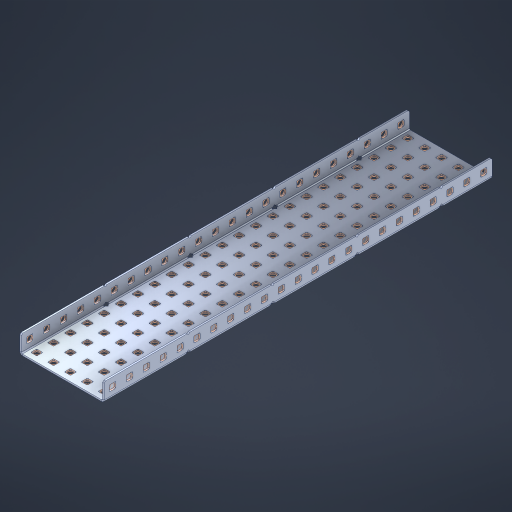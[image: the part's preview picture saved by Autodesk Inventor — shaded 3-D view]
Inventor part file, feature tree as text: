
AUTODESK INVENTOR PART (.ipt)
format: ipt  version: 2023 (Build 270158000, 158)  size: 1,823,744 bytes
history: native  units: in
note: dims shown in document units (in); Inventor stores cm internally (conversion verified against a paired STEP export)
features: other x166, extrude x160, sheet_metal_op x10, sketch x8, mirror x1, pattern_linear x1, chamfer x1
ambient origin geometry x8: Origin, YZ Plane, XZ Plane, XY Plane, X Axis, Y Axis, Z Axis, Center Point
bodies: Solid1 (feature_tree), Body (feature_tree)
feature tree (347):
  other  "Flange Pattern Plane"
  sheet_metal_op  "Flange Pattern"
  sheet_metal_op  "Body Pattern"
  other  "Arc Length"
  mirror  "Notch Mirror"
  pattern_linear  "Notch Pattern"  Spacing1=0.1875in  [1 undecoded]
  chamfer  "End Chamfer"
  extrude  "Half Cut"  Depth=0.0469in
  sketch  "Sketch1"  dims[d0=2.5in]
  other  "Plate1"
  sketch  "Sketch2"  dims[d1=11.5in]
  other  "Plate2"
  sheet_metal_op  "Bend1"
  sheet_metal_op  "Corner1"
  sketch  "Sketch3"  dims[d2=0.0469in]
  other  "Flange Pattern Sketch"
  sketch  "Sketch7"  dims[d3=0.0469in]
  other  "Srf1"
  other  "Srf2"
  sketch  "Sketch8"  dims[d4=0.0234in]
  sketch  "Sketch9"  dims[d5=0.0938in]
  other  "Srf91"
  sheet_metal_op  "Body Pattern Sketch"
  other  "Srf92"
  sketch  "Sketch13"  dims[d6=0.0469in]
  sketch  "Sketch14"  dims[d7=0.5in d8=90.0deg d9=0.0312in d10=0.1875in d11=0.0469in d12=0.0469in d16=0.182in d17=0.02in d18=0.0469in d19=0.0in d20=0.25in d21=0.25in d46=0.172in d47=1.0in d48=0.0in d49=0.182in d50=0.02in d51=0.25in d52=0.25in d53=0.0469in d54=0.0in d55=0.172in d56=1.0in d57=0.0in d60=9.0551in d62=0.5in d63=1.9685in d65=0.5in d85=0.1227in d86=0.1659in d88=0.04in d89=0.0469in d90=0.0in d91=0.04in d92=0.0491in d95=2.5in d96=0.04in d97=0.25in d98=45.0deg d101=0.0in d102=2.497in d131=2.5in d132=9.0551in d134=0.5in d139=0.5in]
  other  "Srf856"
  other  "Srf1310"
  other  "Srf1311"
  other  "Srf1312"
  other  "Srf1376"
  other  "Srf1377"
  other  "Srf1728"
  other  "Srf1755"
  other  "Srf1878"
  other  "Srf1879"
  other  "Srf1880"
  other  "Srf1881"
  other  "Srf1882"
  other  "Srf1883"
  other  "Srf1884"
  other  "Srf1885"
  other  "Srf1886"
  other  "Srf1887"
  other  "Srf1888"
  other  "Srf1889"
  other  "Srf1890"
  other  "Srf1891"
  other  "Srf1892"
  other  "Srf1893"
  other  "Srf1894"
  other  "Srf1895"
  other  "Srf1896"
  other  "Srf1897"
  other  "Srf1898"
  other  "Srf1899"
  other  "Srf1900"
  other  "Srf1901"
  other  "Srf1902"
  other  "Srf1903"
  other  "Srf1904"
  other  "Srf1905"
  other  "Srf1906"
  other  "Srf1942"
  other  "Srf1943"
  other  "Srf1944"
  other  "Srf1945"
  other  "Srf1946"
  other  "Srf1947"
  other  "Srf1948"
  other  "Srf1949"
  other  "Srf1950"
  other  "Srf1951"
  other  "Srf1952"
  other  "Srf1953"
  other  "Srf1954"
  other  "Srf1955"
  other  "Srf1956"
  other  "Srf1957"
  other  "Srf1958"
  other  "Srf1959"
  other  "Srf1960"
  other  "Srf1961"
  other  "Srf1962"
  other  "Srf1963"
  other  "Srf1964"
  other  "Srf1965"
  other  "Srf1966"
  other  "Srf1967"
  other  "Srf1968"
  other  "Srf1969"
  other  "Srf1970"
  other  "Srf2111"
  other  "Srf2112"
  other  "Srf2113"
  other  "Srf2114"
  other  "Srf2115"
  other  "Srf2116"
  other  "Srf2117"
  other  "Srf2118"
  other  "Srf2119"
  other  "Srf2120"
  other  "Srf2121"
  other  "Srf2146"
  other  "Srf2147"
  other  "Srf2148"
  other  "Srf2149"
  other  "Srf2150"
  other  "Srf2151"
  other  "Srf2152"
  other  "Srf2153"
  other  "Srf2154"
  other  "Srf2155"
  other  "Srf2156"
  other  "Srf2157"
  other  "Srf2158"
  other  "Srf2159"
  other  "Srf2160"
  other  "Srf2161"
  other  "Srf2162"
  other  "Srf2163"
  other  "Srf2164"
  other  "Srf2165"
  other  "Srf2166"
  other  "Srf2167"
  other  "Srf2168"
  other  "Srf2169"
  other  "Srf2170"
  other  "Srf2171"
  other  "Srf2172"
  other  "Srf2173"
  other  "Srf2174"
  other  "Srf2175"
  other  "Srf2176"
  other  "Srf2177"
  other  "Srf2178"
  other  "Srf2179"
  other  "Srf2180"
  other  "Srf2181"
  other  "Srf2182"
  other  "Srf2183"
  other  "Srf2184"
  other  "Srf2185"
  other  "Srf2186"
  other  "Srf2187"
  other  "Srf2188"
  other  "Srf2189"
  other  "Srf2190"
  other  "Srf2191"
  other  "Srf2192"
  other  "Srf2193"
  other  "Srf2194"
  other  "Srf2195"
  other  "Srf2196"
  other  "Srf2197"
  other  "Srf2198"
  other  "Srf2199"
  other  "Srf2200"
  other  "Srf2201"
  other  "Srf2202"
  other  "Srf2203"
  other  "Srf2204"
  other  "Srf2205"
  other  "Srf2206"
  other  "Srf2207"
  other  "Srf2208"
  other  "Srf2209"
  other  "Srf2210"
  other  "Srf2211"
  other  "Srf2212"
  other  "Srf2213"
  other  "Srf2214"
  other  "Srf2215"
  other  "Srf2216"
  other  "Srf2217"
  other  "Srf2218"
  other  "Srf2219"
  other  "Srf2220"
  other  "Srf2221"
  other  "Srf2222"
  other  "Srf2223"
  other  "Srf2224"
  other  "Srf2225"
  sheet_metal_op  "Flange Stamp"
  sheet_metal_op  "Flange Circle"
  sheet_metal_op  "Body Stamp"
  sheet_metal_op  "Body Circle"
  sheet_metal_op  "Notch"
  extrude  "ExtrusionSrf2"  Depth=0.0469in
  extrude  "ExtrusionSrf92"  Depth=2.5in
  extrude  "ExtrusionSrf856"  Depth=0.02in
  extrude  "ExtrusionSrf1310"  Depth=0.0469in
  extrude  "ExtrusionSrf1311"  TaperAngle=0.0deg  [1 undecoded]
  extrude  "ExtrusionSrf1312"  Depth=0.25in
  extrude  "ExtrusionSrf1376"  Depth=0.25in
  extrude  "ExtrusionSrf1377"  Depth=2.5in
  extrude  "ExtrusionSrf1728"  Depth=2.5in TaperAngle=0.0deg
  extrude  "ExtrusionSrf1755"  Depth=2.5in
  extrude  "ExtrusionSrf1878"  Depth=0.02in
  extrude  "ExtrusionSrf1879"  Depth=0.25in
  extrude  "ExtrusionSrf1880"  Depth=0.25in
  extrude  "ExtrusionSrf1881"  Depth=0.0469in
  extrude  "ExtrusionSrf1882"  TaperAngle=0.0deg  [1 undecoded]
  extrude  "ExtrusionSrf1883"  Depth=2.5in
  extrude  "ExtrusionSrf1884"  Depth=2.5in TaperAngle=0.0deg
  extrude  "ExtrusionSrf1885"  Depth=2.5in
  extrude  "ExtrusionSrf1886"  Depth=2.5in
  extrude  "ExtrusionSrf1887"  Depth=2.5in
  extrude  "ExtrusionSrf1888"  Depth=2.5in
  extrude  "ExtrusionSrf1889"  Depth=2.5in
  extrude  "ExtrusionSrf1890"  Depth=0.0469in
  extrude  "ExtrusionSrf1891"  TaperAngle=0.0deg  [1 undecoded]
  extrude  "ExtrusionSrf1892"  Depth=2.5in
  extrude  "ExtrusionSrf1893"  Depth=2.5in
  extrude  "ExtrusionSrf1894"  Depth=2.5in
  extrude  "ExtrusionSrf1895"  Depth=0.25in TaperAngle=45.0deg
  extrude  "ExtrusionSrf1896"  TaperAngle=0.0deg  [1 undecoded]
  extrude  "ExtrusionSrf1897"  Depth=2.5in
  extrude  "ExtrusionSrf1898"  Depth=2.5in
  extrude  "ExtrusionSrf1899"  Depth=2.5in
  extrude  "ExtrusionSrf1900"  Depth=2.5in
  extrude  "ExtrusionSrf1901"  Depth=2.5in
  extrude  "ExtrusionSrf1902"  [1 undecoded]
  extrude  "ExtrusionSrf1903"  [1 undecoded]
  extrude  "ExtrusionSrf1904"  [1 undecoded]
  extrude  "ExtrusionSrf1905"  [1 undecoded]
  extrude  "ExtrusionSrf1906"  [1 undecoded]
  extrude  "ExtrusionSrf1942"  [1 undecoded]
  extrude  "ExtrusionSrf1943"  [1 undecoded]
  extrude  "ExtrusionSrf1944"  [1 undecoded]
  extrude  "ExtrusionSrf1945"  [1 undecoded]
  extrude  "ExtrusionSrf1946"  [1 undecoded]
  extrude  "ExtrusionSrf1947"  [1 undecoded]
  extrude  "ExtrusionSrf1948"  [1 undecoded]
  extrude  "ExtrusionSrf1949"  [1 undecoded]
  extrude  "ExtrusionSrf1950"  [1 undecoded]
  extrude  "ExtrusionSrf1951"  [1 undecoded]
  extrude  "ExtrusionSrf1952"  [1 undecoded]
  extrude  "ExtrusionSrf1953"  [1 undecoded]
  extrude  "ExtrusionSrf1954"  [1 undecoded]
  extrude  "ExtrusionSrf1955"  [1 undecoded]
  extrude  "ExtrusionSrf1956"  [1 undecoded]
  extrude  "ExtrusionSrf1957"  [1 undecoded]
  extrude  "ExtrusionSrf1958"  [1 undecoded]
  extrude  "ExtrusionSrf1959"  [1 undecoded]
  extrude  "ExtrusionSrf1960"  [1 undecoded]
  extrude  "ExtrusionSrf1961"  [1 undecoded]
  extrude  "ExtrusionSrf1962"  [1 undecoded]
  extrude  "ExtrusionSrf1963"  [1 undecoded]
  extrude  "ExtrusionSrf1964"  [1 undecoded]
  extrude  "ExtrusionSrf1965"  [1 undecoded]
  extrude  "ExtrusionSrf1966"  [1 undecoded]
  extrude  "ExtrusionSrf1967"  [1 undecoded]
  extrude  "ExtrusionSrf1968"  [1 undecoded]
  extrude  "ExtrusionSrf1969"  [1 undecoded]
  extrude  "ExtrusionSrf1970"  [1 undecoded]
  extrude  "ExtrusionSrf2111"  [1 undecoded]
  extrude  "ExtrusionSrf2112"  [1 undecoded]
  extrude  "ExtrusionSrf2113"  [1 undecoded]
  extrude  "ExtrusionSrf2114"  [1 undecoded]
  extrude  "ExtrusionSrf2115"  [1 undecoded]
  extrude  "ExtrusionSrf2116"  [1 undecoded]
  extrude  "ExtrusionSrf2117"  [1 undecoded]
  extrude  "ExtrusionSrf2118"  [1 undecoded]
  extrude  "ExtrusionSrf2119"  [1 undecoded]
  extrude  "ExtrusionSrf2120"  [1 undecoded]
  extrude  "ExtrusionSrf2121"  [1 undecoded]
  extrude  "ExtrusionSrf2146"  [1 undecoded]
  extrude  "ExtrusionSrf2147"  [1 undecoded]
  extrude  "ExtrusionSrf2148"  [1 undecoded]
  extrude  "ExtrusionSrf2149"  [1 undecoded]
  extrude  "ExtrusionSrf2150"  [1 undecoded]
  extrude  "ExtrusionSrf2151"  [1 undecoded]
  extrude  "ExtrusionSrf2152"  [1 undecoded]
  extrude  "ExtrusionSrf2153"  [1 undecoded]
  extrude  "ExtrusionSrf2154"  [1 undecoded]
  extrude  "ExtrusionSrf2155"  [1 undecoded]
  extrude  "ExtrusionSrf2156"  [1 undecoded]
  extrude  "ExtrusionSrf2157"  [1 undecoded]
  extrude  "ExtrusionSrf2158"  [1 undecoded]
  extrude  "ExtrusionSrf2159"  [1 undecoded]
  extrude  "ExtrusionSrf2160"  [1 undecoded]
  extrude  "ExtrusionSrf2161"  [1 undecoded]
  extrude  "ExtrusionSrf2162"  [1 undecoded]
  extrude  "ExtrusionSrf2163"  [1 undecoded]
  extrude  "ExtrusionSrf2164"  [1 undecoded]
  extrude  "ExtrusionSrf2165"  [1 undecoded]
  extrude  "ExtrusionSrf2166"  [1 undecoded]
  extrude  "ExtrusionSrf2167"  [1 undecoded]
  extrude  "ExtrusionSrf2168"  [1 undecoded]
  extrude  "ExtrusionSrf2169"  [1 undecoded]
  extrude  "ExtrusionSrf2170"  [1 undecoded]
  extrude  "ExtrusionSrf2171"  [1 undecoded]
  extrude  "ExtrusionSrf2172"  [1 undecoded]
  extrude  "ExtrusionSrf2173"  [1 undecoded]
  extrude  "ExtrusionSrf2174"  [1 undecoded]
  extrude  "ExtrusionSrf2175"  [1 undecoded]
  extrude  "ExtrusionSrf2176"  [1 undecoded]
  extrude  "ExtrusionSrf2177"  [1 undecoded]
  extrude  "ExtrusionSrf2178"  [1 undecoded]
  extrude  "ExtrusionSrf2179"  [1 undecoded]
  extrude  "ExtrusionSrf2180"  [1 undecoded]
  extrude  "ExtrusionSrf2181"  [1 undecoded]
  extrude  "ExtrusionSrf2182"  [1 undecoded]
  extrude  "ExtrusionSrf2183"  [1 undecoded]
  extrude  "ExtrusionSrf2184"  [1 undecoded]
  extrude  "ExtrusionSrf2185"  [1 undecoded]
  extrude  "ExtrusionSrf2186"  [1 undecoded]
  extrude  "ExtrusionSrf2187"  [1 undecoded]
  extrude  "ExtrusionSrf2188"  [1 undecoded]
  extrude  "ExtrusionSrf2189"  [1 undecoded]
  extrude  "ExtrusionSrf2190"  [1 undecoded]
  extrude  "ExtrusionSrf2191"  [1 undecoded]
  extrude  "ExtrusionSrf2192"  [1 undecoded]
  extrude  "ExtrusionSrf2193"  [1 undecoded]
  extrude  "ExtrusionSrf2194"  [1 undecoded]
  extrude  "ExtrusionSrf2195"  [1 undecoded]
  extrude  "ExtrusionSrf2196"  [1 undecoded]
  extrude  "ExtrusionSrf2197"  [1 undecoded]
  extrude  "ExtrusionSrf2198"  [1 undecoded]
  extrude  "ExtrusionSrf2199"  [1 undecoded]
  extrude  "ExtrusionSrf2200"  [1 undecoded]
  extrude  "ExtrusionSrf2201"  [1 undecoded]
  extrude  "ExtrusionSrf2202"  [1 undecoded]
  extrude  "ExtrusionSrf2203"  [1 undecoded]
  extrude  "ExtrusionSrf2204"  [1 undecoded]
  extrude  "ExtrusionSrf2205"  [1 undecoded]
  extrude  "ExtrusionSrf2206"  [1 undecoded]
  extrude  "ExtrusionSrf2207"  [1 undecoded]
  extrude  "ExtrusionSrf2208"  [1 undecoded]
  extrude  "ExtrusionSrf2209"  [1 undecoded]
  extrude  "ExtrusionSrf2210"  [1 undecoded]
  extrude  "ExtrusionSrf2211"  [1 undecoded]
  extrude  "ExtrusionSrf2212"  [1 undecoded]
  extrude  "ExtrusionSrf2213"  [1 undecoded]
  extrude  "ExtrusionSrf2214"  [1 undecoded]
  extrude  "ExtrusionSrf2215"  [1 undecoded]
  extrude  "ExtrusionSrf2216"  [1 undecoded]
  extrude  "ExtrusionSrf2217"  [1 undecoded]
  extrude  "ExtrusionSrf2218"  [1 undecoded]
  extrude  "ExtrusionSrf2219"  [1 undecoded]
  extrude  "ExtrusionSrf2220"  [1 undecoded]
  extrude  "ExtrusionSrf2221"  [1 undecoded]
  extrude  "ExtrusionSrf2222"  [1 undecoded]
  extrude  "ExtrusionSrf2223"  [1 undecoded]
  extrude  "ExtrusionSrf2224"  [1 undecoded]
  extrude  "ExtrusionSrf2225"  [1 undecoded]
note: 130 required parameter values undecoded (feature->parameter linkage not recoverable at this tier; creation-order binding heuristic only, values carry confidence <= 0.55)
